# Revit family: 0042524 Sylvania Lighting Fixture ISOLINE  1690MM 4K DASY 5C
name_source: partatom
category: Lighting Fixtures
revit_build: Autodesk Revit 2018 (Build: 20170223_1515(x64)
units: mm (PartAtom-declared; Revit-internal decimal feet)

## family parameters
Cut with Voids When Loaded = No
Host = Face
Light Source = Yes
OmniClass Number = 23.80.70.00
OmniClass Title = Lighting
Part Type = Normal
Room Calculation Point = No
Round Connector Dimension = Use Diameter
Shared = No

## types (1)
- 0042524 ISOLINE  1690MM 4K DASY 5C
    Apparent Load = 57 VA
    Assembly Code = D5020200
    AssetType = Fixed
    ClassificationName = Uniclass2015
    ClassificationValue = EF_70_80
    Color Filter = 16777215
    Cost = 0 $
    Default Elevation = 1219 mm
    Description = Isoline LED linear luminaire for industrial and commercial applications. 1690 mm lenght with double asymmetrical optics provide homogenous light distribution for wide, shelf areas. Aluminium housing, RAL 9016. Max + 35 °C operating temperature range, 4000 K, CRI 80, UGR <25, 3 SDMC. 57 W power consumption, 8300 lm luminous flux, 145 lm/W efficacy, 1690 mm x 62 mm x 59 mm (L x W x H) dimensions, IP20, IK03, 220-240 V 50/60 Hz, Class I.Lifespan L70:B50 60,000 hours.
    Dimming Lamp Color Temperature Shift = <None>
    DocumentationLiterature = http://www.sylvania-lighting.com
    DurationUnit = hours
    ElectricShockClassification = 145
    Emit Shape Visible in Rendering = No
    Emit from Circle Diameter = 610 mm
    ExpectedLife = 50000
    Height = 1000 mm  [stored 3.28084 ft]
    IfcExportAs = Class I
    IfcExportType = IfcLightFixtureType
    ImpactProtectionIndex = IfcLightFixtureType
    IngressProtection = IfcLightFixtureType
    InputNominalFrequency = 4000
    InputVoltage = 0
    LampColourRenderingIndex = 16500
    LampColourTemperature = LED
    LampMacAdamStep = 80
    LampNominalLuminous = 4000 K
    Length = 1690 mm  [stored 5.54462 ft]
    LightOutputRatio = LED
    LuminaireType = 0
    ManufacturerName = 145 lm/W
    Material = Feilo Sylvania
    Material_1_FEILO = <By Category>
    Material_2_FEILO = <By Category>
    Material_3_FEILO = <By Category>
    Material_4_FEILO = <By Category>
    Model = ISOLINE  1690MM 4K DASY 5C
    ModelNumber = 0042524
    ModelReference = ISOLINE  1690MM 4K DASY 5C
    Name = ISOLINE  1690MM 4K DASY 5C
    NominalDepth = 0 mm  [stored 0 ft]
    NominalHeight = 0 mm  [stored 0 ft]
    NominalLength = 62 mm
    Photometric Web File = 0042524.ies
    PowerConsumption = Lighting
    PowerFactor = 0
    Tilt Angle = 90.00°
    Type Image = <None>
    TypeName = ISOLINE  1690MM 4K DASY 5C
    URL = 0
    Voltage = 0 V
    WarrantyDescription = http://www.sylvania-lighting.com
    Width = 62 mm
    height = 59 mm
    spacer centres = 1000 mm  [stored 3.28084 ft]
    spacer height = 5 mm  [stored 0.0164042 ft]
    suspension height = 1000 mm  [stored 3.28084 ft]

note: [stored X ft] marks values corroborated as IEEE doubles in the binary element streams (Revit-internal decimal feet)

## geometry (parser evidence)
native form markers: Sweep x3
no freeform markers — native parametric forms only
